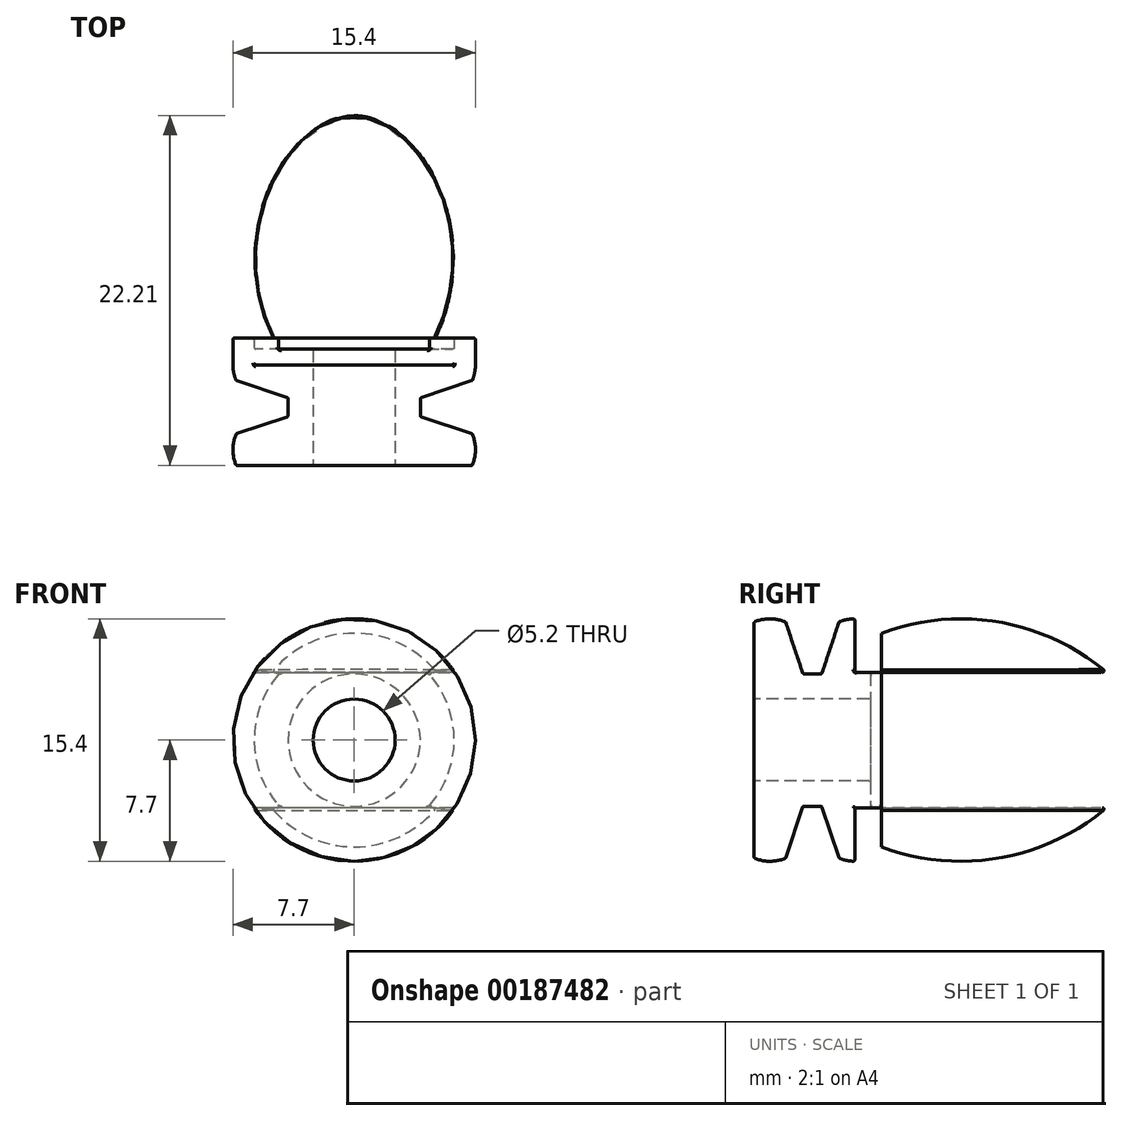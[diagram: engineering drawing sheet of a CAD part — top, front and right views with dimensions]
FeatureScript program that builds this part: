
annotation { "Feature Type Name" : "Feature", "Feature Type Description" : "" }
export const myFeature = defineFeature(function(context is Context, id is Id, definition is map)
    precondition{}
    {
        {
            var Q0;
            Q0=qCreatedBy(makeId("Front.planeOp"),FACE);
            var sketch = newSketch(context, id + "F0", { "sketchPlane" : qUnion([Q0])});
            skCircle(sketch, "E0", {"center": v(0, 0) * mm, "radius": 7.7 * mm});
            skCircle(sketch, "E1", {"center": v(0, 0) * mm, "radius": 2.6 * mm});
            skSolve(sketch);
        }
        {
            var Q0;
            Q0=qCreatedBy(makeId("Right.planeOp"),FACE);
            var sketch = newSketch(context, id + "F1", { "sketchPlane" : qUnion([Q0])});
            skLineSegment(sketch, "E2.0", {"start": v(0, -7.7) * mm, "end": v(0, 7.7) * mm, "construction": true});
            skLineSegment(sketch, "E3", {"start": v(-1.7, 7.5) * mm, "end": v(-1.7, 0) * mm});
            skLineSegment(sketch, "E4", {"start": v(-0.6, 4.2) * mm, "end": v(-0.6, 0) * mm});
            skArc(sketch, "E5", {"start": v(-1.7, 7.5) * mm, "mid": v(-2.7, 7.7) * mm, "end": v(-3.7, 7.5) * mm});
            skLineSegment(sketch, "E6", {"start": v(-0.6, 4.2) * mm, "end": v(-1.7, 7.5) * mm});
            skLineSegment(sketch, "E7", {"start": v(-12.72, 7.7) * mm, "end": v(9.43, 7.7) * mm, "construction": true});
            skLineSegment(sketch, "E8", {"start": v(-12.28, -7.7) * mm, "end": v(13.59, -7.7) * mm, "construction": true});
            skLineSegment(sketch, "E9", {"start": v(-12.4, 0) * mm, "end": v(13.31, 0) * mm, "construction": true});
            skLineSegment(sketch, "E10", {"start": v(-0.6, 4.2) * mm, "end": v(0, 4.2) * mm});
            skLineSegment(sketch, "E11", {"start": v(-3.7, 7.5) * mm, "end": v(-3.7, 0) * mm});
            skLineSegment(sketch, "E12.MirrorCS", {"start": v(0.6, 4.2) * mm, "end": v(0, 4.2) * mm});
            skLineSegment(sketch, "E13.MirrorCS", {"start": v(0.6, 4.2) * mm, "end": v(0.6, 0) * mm});
            skLineSegment(sketch, "E14.MirrorCS", {"start": v(0.6, 4.2) * mm, "end": v(1.7, 7.5) * mm});
            skLineSegment(sketch, "E15.MirrorCS", {"start": v(1.7, 7.5) * mm, "end": v(1.7, 0) * mm});
            skArc(sketch, "E16.MirrorCS", {"start": v(1.7, 7.5) * mm, "mid": v(2.7, 7.7) * mm, "end": v(3.7, 7.5) * mm});
            skLineSegment(sketch, "E17.MirrorCS", {"start": v(3.7, 7.5) * mm, "end": v(3.7, 0) * mm});
            skLineSegment(sketch, "E18", {"start": v(-3.7, 0) * mm, "end": v(-1.7, 0) * mm});
            skLineSegment(sketch, "E19", {"start": v(-1.7, 0) * mm, "end": v(-0.6, 0) * mm});
            skLineSegment(sketch, "E20", {"start": v(-0.6, 0) * mm, "end": v(0, 0) * mm});
            skLineSegment(sketch, "E21.MirrorCS", {"start": v(0.6, 0) * mm, "end": v(0, 0) * mm});
            skLineSegment(sketch, "E22.MirrorCS", {"start": v(3.7, 0) * mm, "end": v(1.7, 0) * mm});
            skLineSegment(sketch, "E23.MirrorCS", {"start": v(1.7, 0) * mm, "end": v(0.6, 0) * mm});
            skPoint(sketch, "E24", {"position": v(3.7, 6.5) * mm});
            skLineSegment(sketch, "E25", {"start": v(3.7, 4.3) * mm, "end": v(18.7, 4.3) * mm});
            skPoint(sketch, "E26", {"position": v(9.43, 7.7) * mm});
            skPoint(sketch, "E27", {"position": v(18.7, 4.3) * mm});
            skArc(sketch, "E28", {"start": v(18.7, 4.3) * mm, "mid": v(11.5, 7.55) * mm, "end": v(3.7, 6.5) * mm});
            skSolve(sketch);
        }
        {
            var Q0;
            Q0 = qSketchRegion(id + "F1", true);
            var Q1;
            Q1=sQuery(id+"F1.wireOp",EDGE,"E9");
            revolve(context, id + "F2", {"entities" : qUnion([Q0]), "axis" : qUnion([Q1]), "revolveType" : RevolveType.FULL});
        }
        {
            var Q0;
            Q0=qCreatedBy(makeId("Right.planeOp"),FACE);
            var sketch = newSketch(context, id + "F3", { "sketchPlane" : qUnion([Q0])});
            skPoint(sketch, "E29.0", {"position": v(18.7, 4.3) * mm});
            skLineSegment(sketch, "E30", {"start": v(18.7, 4.3) * mm, "end": v(18.7, 0) * mm});
            skLineSegment(sketch, "E31", {"start": v(18.7, 4.3) * mm, "end": v(3.7, 4.3) * mm});
            skPoint(sketch, "E32.0", {"position": v(3.7, 4.3) * mm});
            skPoint(sketch, "E33.0", {"position": v(3.7, 0) * mm});
            skLineSegment(sketch, "E34", {"start": v(3.7, 4.3) * mm, "end": v(3.7, 0) * mm});
            skLineSegment(sketch, "E35.MirrorCS", {"start": v(3.7, -4.3) * mm, "end": v(3.7, 0) * mm});
            skLineSegment(sketch, "E36.MirrorCS", {"start": v(18.7, -4.3) * mm, "end": v(3.7, -4.3) * mm});
            skLineSegment(sketch, "E37.MirrorCS", {"start": v(18.7, -4.3) * mm, "end": v(18.7, 0) * mm});
            skSolve(sketch);
        }
        {
            var Q0;
            Q0 = qSketchRegion(id + "F3", true);
            extrude(context, id + "F4", {"entities" : qUnion([Q0]), "operationType" : NewBodyOperationType.REMOVE, "endBound" : BoundingType.THROUGH_ALL, "oppositeDirection" : true, "depth" : 25 * mm, "hasSecondDirection" : true, "secondDirectionBound" : SecondDirectionBoundingType.THROUGH_ALL, "secondDirectionOppositeDirection" : false, "secondDirectionDepth" : 25 * mm});
        }
        {
            var Q0;
            Q0=qCreatedBy(makeId("Right.planeOp"),FACE);
            var sketch = newSketch(context, id + "F5", { "sketchPlane" : qUnion([Q0])});
            skPoint(sketch, "E38.0", {"position": v(2.7, 7.7) * mm});
            skPoint(sketch, "E39.0", {"position": v(1.7, 7.5) * mm});
            skLineSegment(sketch, "E40", {"start": v(2.7, 7.7) * mm, "end": v(4.4, 7.7) * mm});
            skLineSegment(sketch, "E41", {"start": v(4.4, 7.7) * mm, "end": v(4.4, 6.35) * mm});
            skLineSegment(sketch, "E42", {"start": v(4.4, 6.35) * mm, "end": v(2.7, 6.35) * mm});
            skLineSegment(sketch, "E43", {"start": v(2.7, 6.35) * mm, "end": v(2.7, 7.7) * mm});
            skSolve(sketch);
        }
        {
            var Q0;
            Q0 = qSketchRegion(id + "F5", true);
            var Q1;
            Q1=sQuery(id+"F1.wireOp",EDGE,"E9");
            revolve(context, id + "F6", {"entities" : qUnion([Q0]), "axis" : qUnion([Q1]), "revolveType" : RevolveType.FULL});
        }
        {
            var Q0;
            Q0=qCreatedBy(makeId("Right.planeOp"),FACE);
            var sketch = newSketch(context, id + "F7", { "sketchPlane" : qUnion([Q0])});
            skPoint(sketch, "E44.0", {"position": v(3.7, 4.3) * mm});
            skPoint(sketch, "E45.0", {"position": v(2.7, 7.7) * mm});
            skPoint(sketch, "E46.0", {"position": v(4.4, 7.7) * mm});
            skLineSegment(sketch, "E47", {"start": v(2.7, 7.7) * mm, "end": v(4.4, 7.7) * mm});
            skLineSegment(sketch, "E48", {"start": v(4.4, 4.3) * mm, "end": v(2.7, 4.3) * mm});
            skLineSegment(sketch, "E49", {"start": v(2.7, 4.3) * mm, "end": v(2.7, 7.7) * mm});
            skLineSegment(sketch, "E50", {"start": v(4.4, 7.7) * mm, "end": v(4.4, 4.3) * mm});
            skLineSegment(sketch, "E51.MirrorCS", {"start": v(4.4, -7.7) * mm, "end": v(4.4, -4.3) * mm});
            skLineSegment(sketch, "E52.MirrorCS", {"start": v(4.4, -4.3) * mm, "end": v(2.7, -4.3) * mm});
            skLineSegment(sketch, "E53.MirrorCS", {"start": v(2.7, -4.3) * mm, "end": v(2.7, -7.7) * mm});
            skLineSegment(sketch, "E54.MirrorCS", {"start": v(2.7, -7.7) * mm, "end": v(4.4, -7.7) * mm});
            skSolve(sketch);
        }
        {
            var Q0;
            Q0 = qSketchRegion(id + "F7", true);
            extrude(context, id + "F8", {"entities" : qUnion([Q0]), "operationType" : NewBodyOperationType.REMOVE, "endBound" : BoundingType.THROUGH_ALL, "depth" : 25 * mm, "hasSecondDirection" : true, "secondDirectionBound" : SecondDirectionBoundingType.THROUGH_ALL, "secondDirectionOppositeDirection" : true, "secondDirectionDepth" : 25 * mm});
        }
        {
            var Q0;
            Q0=makeQuery(id+"F2.opRevolve","SWEPT_BODY",BODY,{"disambiguationData":[OSD([sQuery(id+"F1.wireOp",EDGE,"E5"),sQuery(id+"F1.wireOp",EDGE,"E6"),sQuery(id+"F1.wireOp",EDGE,"E10"),sQuery(id+"F1.wireOp",EDGE,"E11"),sQuery(id+"F1.wireOp",EDGE,"E12.MirrorCS"),sQuery(id+"F1.wireOp",EDGE,"E14.MirrorCS"),sQuery(id+"F1.wireOp",EDGE,"E16.MirrorCS"),sQuery(id+"F1.wireOp",EDGE,"E17.MirrorCS"),sQuery(id+"F1.wireOp",EDGE,"E18"),sQuery(id+"F1.wireOp",EDGE,"E19"),sQuery(id+"F1.wireOp",EDGE,"E20"),sQuery(id+"F1.wireOp",EDGE,"E21.MirrorCS"),sQuery(id+"F1.wireOp",EDGE,"E22.MirrorCS"),sQuery(id+"F1.wireOp",EDGE,"E23.MirrorCS"),sQuery(id+"F1.wireOp",EDGE,"E25"),sQuery(id+"F1.wireOp",EDGE,"E28")])]});
            var Q1;
            Q1=makeQuery(id+"F8.boolean.opBoolean","SPLIT",BODY,{"disambiguationData":[OD(1.0)],"derivedFrom":makeQuery(id+"F6.opRevolve","SWEPT_BODY",BODY,{"disambiguationData":[OSD([sQuery(id+"F5.wireOp",EDGE,"E40"),sQuery(id+"F5.wireOp",EDGE,"E41"),sQuery(id+"F5.wireOp",EDGE,"E42"),sQuery(id+"F5.wireOp",EDGE,"E43")])]})});
            var Q2;
            Q2=makeQuery(id+"F8.boolean.opBoolean","SPLIT",BODY,{"disambiguationData":[OD(0.0)],"derivedFrom":makeQuery(id+"F6.opRevolve","SWEPT_BODY",BODY,{"disambiguationData":[OSD([sQuery(id+"F5.wireOp",EDGE,"E40"),sQuery(id+"F5.wireOp",EDGE,"E41"),sQuery(id+"F5.wireOp",EDGE,"E42"),sQuery(id+"F5.wireOp",EDGE,"E43")])]})});
            booleanBodies(context, id + "F9", {"operationType" : BooleanOperationType.UNION, "tools" : qUnion([Q0, Q1, Q2])});
        }
        {
            var Q0;
            Q0=makeQuery(id+"F0.imprint","IMPRINT",FACE,{"disambiguationData":[TD([[makeQuery(id+"F0.imprint","IMPRINT",EDGE,{"derivedFrom":sQuery(id+"F0.wireOp",EDGE,"E1")}),1.0]])]});
            extrude(context, id + "F10", {"entities" : qUnion([Q0]), "operationType" : NewBodyOperationType.REMOVE, "endBound" : BoundingType.THROUGH_ALL, "oppositeDirection" : true, "depth" : 25 * mm, "hasSecondDirection" : true, "secondDirectionBound" : SecondDirectionBoundingType.THROUGH_ALL, "secondDirectionOppositeDirection" : false, "secondDirectionDepth" : 25 * mm});
        }
        {
            var Q0;
            {var subQ0=sQuery(id+"F1.wireOp",EDGE,"E16.MirrorCS");var subQ2=makeQuery(id+"F8.opExtrude","SWEPT_FACE",FACE,{"disambiguationData":[OSD([sQuery(id+"F7.wireOp",EDGE,"E48")])]});var subQ3=sQuery(id+"F1.wireOp",EDGE,"E17.MirrorCS");Q0=makeQuery(id+"F9.opBoolean","SPLIT",FACE,{"disambiguationData":[TD([makeQuery(id+"F8.boolean.opBoolean","COPY",FACE,{"disambiguationData":[OD(0.0)],"derivedFrom":subQ2})])],"derivedFrom":makeQuery(id+"F4.boolean.opBoolean","MERGE",FACE,{"derivedFrom":[makeQuery(id+"F2.opRevolve","SWEPT_FACE",FACE,{"disambiguationData":[OSD([subQ3]),TDD([makeQuery(id+"F1.imprint","IMPRINT",EDGE,{"disambiguationData":[TD([[makeQuery(id+"F1.imprint","INTERSECT",VERTEX,{"derivedFrom":[subQ0,subQ3]}),-1.0]])],"derivedFrom":subQ3})])]}),makeQuery(id+"F2.opRevolve","SWEPT_FACE",FACE,{"disambiguationData":[OSD([subQ3]),TDD([makeQuery(id+"F1.imprint","IMPRINT",EDGE,{"disambiguationData":[TD([[makeQuery(id+"F1.imprint","INTERSECT",VERTEX,{"derivedFrom":[subQ3,sQuery(id+"F1.wireOp",EDGE,"E22.MirrorCS")]}),1.0]])],"derivedFrom":subQ3})])]}),makeQuery(id+"F4.opExtrude","SWEPT_FACE",FACE,{"disambiguationData":[OSD([sQuery(id+"F3.wireOp",EDGE,"E34"),sQuery(id+"F3.wireOp",EDGE,"E35.MirrorCS")])]})]})});}
            var Q1;
            Q1=makeQuery(id+"F2.opRevolve","SWEPT_FACE",FACE,{"disambiguationData":[OSD([sQuery(id+"F1.wireOp",EDGE,"E16.MirrorCS")])]});
            var Q2;
            Q2=makeQuery(id+"F8.boolean.opBoolean","SPLIT",FACE,{"disambiguationData":[OD(1.0)],"derivedFrom":makeQuery(id+"F6.opRevolve","SWEPT_FACE",FACE,{"disambiguationData":[OSD([sQuery(id+"F5.wireOp",EDGE,"E40")])]})});
            var Q3;
            Q3=makeQuery(id+"F8.boolean.opBoolean","COPY",FACE,{"disambiguationData":[OD(1.0)],"derivedFrom":makeQuery(id+"F8.opExtrude","SWEPT_FACE",FACE,{"disambiguationData":[OSD([sQuery(id+"F7.wireOp",EDGE,"E48")])]})});
            var Q4;
            Q4=makeQuery(id+"F8.boolean.opBoolean","SPLIT",FACE,{"disambiguationData":[OD(1.0)],"derivedFrom":makeQuery(id+"F6.opRevolve","SWEPT_FACE",FACE,{"disambiguationData":[OSD([sQuery(id+"F5.wireOp",EDGE,"E41")])]})});
            var Q5;
            {var subQ0=makeQuery(id+"F8.opExtrude","SWEPT_FACE",FACE,{"disambiguationData":[OSD([sQuery(id+"F7.wireOp",EDGE,"E48")])]});var subQ1=makeQuery(id+"F2.opRevolve","SWEPT_FACE",FACE,{"disambiguationData":[OSD([sQuery(id+"F1.wireOp",EDGE,"E28")])]});var subQ2=makeQuery(id+"F4.opExtrude","SWEPT_FACE",FACE,{"disambiguationData":[OSD([sQuery(id+"F3.wireOp",EDGE,"E31")])]});Q5=makeQuery(id+"F9.opBoolean","SPLIT",EDGE,{"disambiguationData":[TD([subQ1,makeQuery(id+"F4.boolean.opBoolean","COPY",FACE,{"derivedFrom":subQ2}),makeQuery(id+"F6.opRevolve","SWEPT_FACE",FACE,{"disambiguationData":[OSD([sQuery(id+"F5.wireOp",EDGE,"E41")])]}),makeQuery(id+"F8.boolean.opBoolean","COPY",FACE,{"disambiguationData":[OD(0.0)],"derivedFrom":subQ0}),makeQuery(id+"F8.boolean.opBoolean","COPY",FACE,{"disambiguationData":[OD(1.0)],"derivedFrom":subQ0})])],"derivedFrom":makeQuery(id+"F4.boolean.opBoolean","INTERSECT",EDGE,{"derivedFrom":[subQ1,subQ2]})});}
            var Q6;
            Q6=makeQuery(id+"F2.opRevolve","SWEPT_EDGE",EDGE,{"disambiguationData":[OSD([sQuery(id+"F1.wireOp",EDGE,"E5"),sQuery(id+"F1.wireOp",EDGE,"E11")])]});
            var Q7;
            Q7=makeQuery(id+"F2.opRevolve","SWEPT_EDGE",EDGE,{"disambiguationData":[OSD([sQuery(id+"F1.wireOp",EDGE,"E14.MirrorCS"),sQuery(id+"F1.wireOp",EDGE,"E15.MirrorCS"),sQuery(id+"F1.wireOp",EDGE,"E16.MirrorCS")])]});
            var Q8;
            Q8=makeQuery(id+"F2.opRevolve","SWEPT_EDGE",EDGE,{"disambiguationData":[OSD([sQuery(id+"F1.wireOp",EDGE,"E3"),sQuery(id+"F1.wireOp",EDGE,"E5"),sQuery(id+"F1.wireOp",EDGE,"E6")])]});
            var Q9;
            Q9=makeQuery(id+"F2.opRevolve","SWEPT_EDGE",EDGE,{"disambiguationData":[OSD([sQuery(id+"F1.wireOp",EDGE,"E4"),sQuery(id+"F1.wireOp",EDGE,"E6"),sQuery(id+"F1.wireOp",EDGE,"E10")])]});
            var Q10;
            Q10=makeQuery(id+"F2.opRevolve","SWEPT_EDGE",EDGE,{"disambiguationData":[OSD([sQuery(id+"F1.wireOp",EDGE,"E12.MirrorCS"),sQuery(id+"F1.wireOp",EDGE,"E13.MirrorCS"),sQuery(id+"F1.wireOp",EDGE,"E14.MirrorCS")])]});
            var Q11;
            Q11=makeQuery(id+"F10.boolean.opBoolean","INTERSECT",EDGE,{"derivedFrom":[makeQuery(id+"F2.opRevolve","SWEPT_FACE",FACE,{"disambiguationData":[OSD([sQuery(id+"F1.wireOp",EDGE,"E11")])]}),makeQuery(id+"F10.opExtrude","SWEPT_FACE",FACE,{"disambiguationData":[OSD([sQuery(id+"F0.wireOp",EDGE,"E1")])]})]});
            var Q12;
            Q12=makeQuery(id+"F9.opBoolean","INTERSECT",EDGE,{"derivedFrom":[makeQuery(id+"F2.opRevolve","SWEPT_FACE",FACE,{"disambiguationData":[OSD([sQuery(id+"F1.wireOp",EDGE,"E16.MirrorCS")])]}),makeQuery(id+"F8.boolean.opBoolean","SPLIT",FACE,{"disambiguationData":[OD(1.0)],"derivedFrom":makeQuery(id+"F6.opRevolve","SWEPT_FACE",FACE,{"disambiguationData":[OSD([sQuery(id+"F5.wireOp",EDGE,"E40")])]})})]});
            var Q13;
            Q13=makeQuery(id+"F8.boolean.opBoolean","SPLIT",EDGE,{"disambiguationData":[OD(1.0)],"derivedFrom":makeQuery(id+"F6.opRevolve","SWEPT_EDGE",EDGE,{"disambiguationData":[OSD([sQuery(id+"F5.wireOp",EDGE,"E40"),sQuery(id+"F5.wireOp",EDGE,"E41")])]})});
            var Q14;
            {var subQ0=sQuery(id+"F1.wireOp",EDGE,"E17.MirrorCS");var subQ1=sQuery(id+"F1.wireOp",EDGE,"E16.MirrorCS");var subQ2=makeQuery(id+"F8.opExtrude","SWEPT_FACE",FACE,{"disambiguationData":[OSD([sQuery(id+"F7.wireOp",EDGE,"E48")])]});Q14=makeQuery(id+"F9.opBoolean","SPLIT",EDGE,{"disambiguationData":[TD([makeQuery(id+"F8.boolean.opBoolean","COPY",FACE,{"disambiguationData":[OD(0.0)],"derivedFrom":subQ2})])],"derivedFrom":makeQuery(id+"F2.opRevolve","SWEPT_EDGE",EDGE,{"disambiguationData":[OSD([subQ1,subQ0])]})});}
            var Q15;
            {var subQ0=sQuery(id+"F1.wireOp",EDGE,"E17.MirrorCS");var subQ1=sQuery(id+"F1.wireOp",EDGE,"E16.MirrorCS");var subQ2=makeQuery(id+"F8.opExtrude","SWEPT_FACE",FACE,{"disambiguationData":[OSD([sQuery(id+"F7.wireOp",EDGE,"E52.MirrorCS")])]});Q15=makeQuery(id+"F9.opBoolean","SPLIT",EDGE,{"disambiguationData":[TD([makeQuery(id+"F8.boolean.opBoolean","COPY",FACE,{"disambiguationData":[OD(0.0)],"derivedFrom":subQ2})])],"derivedFrom":makeQuery(id+"F2.opRevolve","SWEPT_EDGE",EDGE,{"disambiguationData":[OSD([subQ1,subQ0])]})});}
            var Q16;
            {var subQ0=makeQuery(id+"F8.opExtrude","SWEPT_FACE",FACE,{"disambiguationData":[OSD([sQuery(id+"F7.wireOp",EDGE,"E52.MirrorCS")])]});var subQ1=makeQuery(id+"F4.opExtrude","SWEPT_FACE",FACE,{"disambiguationData":[OSD([sQuery(id+"F3.wireOp",EDGE,"E36.MirrorCS")])]});var subQ2=makeQuery(id+"F2.opRevolve","SWEPT_FACE",FACE,{"disambiguationData":[OSD([sQuery(id+"F1.wireOp",EDGE,"E28")])]});Q16=makeQuery(id+"F9.opBoolean","SPLIT",EDGE,{"disambiguationData":[TD([subQ2,makeQuery(id+"F4.boolean.opBoolean","COPY",FACE,{"derivedFrom":subQ1}),makeQuery(id+"F6.opRevolve","SWEPT_FACE",FACE,{"disambiguationData":[OSD([sQuery(id+"F5.wireOp",EDGE,"E41")])]}),makeQuery(id+"F8.boolean.opBoolean","COPY",FACE,{"disambiguationData":[OD(0.0)],"derivedFrom":subQ0}),makeQuery(id+"F8.boolean.opBoolean","COPY",FACE,{"disambiguationData":[OD(1.0)],"derivedFrom":subQ0})])],"derivedFrom":makeQuery(id+"F4.boolean.opBoolean","INTERSECT",EDGE,{"derivedFrom":[subQ2,subQ1]})});}
            var Q17;
            Q17=makeQuery(id+"F4.boolean.opBoolean","COPY",EDGE,{"derivedFrom":makeQuery(id+"F4.opExtrude","SWEPT_EDGE",EDGE,{"disambiguationData":[OSD([sQuery(id+"F3.wireOp",EDGE,"E35.MirrorCS"),sQuery(id+"F3.wireOp",EDGE,"E36.MirrorCS")])]})});
            var Q18;
            Q18=makeQuery(id+"F8.boolean.opBoolean","SPLIT",EDGE,{"disambiguationData":[OD(0.0)],"derivedFrom":makeQuery(id+"F6.opRevolve","SWEPT_EDGE",EDGE,{"disambiguationData":[OSD([sQuery(id+"F5.wireOp",EDGE,"E41"),sQuery(id+"F5.wireOp",EDGE,"E42")])]})});
            var Q19;
            Q19=makeQuery(id+"F8.boolean.opBoolean","SPLIT",EDGE,{"disambiguationData":[OD(1.0)],"derivedFrom":makeQuery(id+"F6.opRevolve","SWEPT_EDGE",EDGE,{"disambiguationData":[OSD([sQuery(id+"F5.wireOp",EDGE,"E41"),sQuery(id+"F5.wireOp",EDGE,"E42")])]})});
            var Q20;
            Q20=makeQuery(id+"F4.boolean.opBoolean","COPY",EDGE,{"derivedFrom":makeQuery(id+"F4.opExtrude","SWEPT_EDGE",EDGE,{"disambiguationData":[OSD([sQuery(id+"F3.wireOp",EDGE,"E31"),sQuery(id+"F3.wireOp",EDGE,"E34")])]})});
            var Q21;
            Q21=makeQuery(id+"F9.opBoolean","INTERSECT",EDGE,{"derivedFrom":[makeQuery(id+"F2.opRevolve","SWEPT_FACE",FACE,{"disambiguationData":[OSD([sQuery(id+"F1.wireOp",EDGE,"E16.MirrorCS")])]}),makeQuery(id+"F8.boolean.opBoolean","SPLIT",FACE,{"disambiguationData":[OD(0.0)],"derivedFrom":makeQuery(id+"F6.opRevolve","SWEPT_FACE",FACE,{"disambiguationData":[OSD([sQuery(id+"F5.wireOp",EDGE,"E40")])]})})]});
            var Q22;
            Q22=makeQuery(id+"F9.opBoolean","INTERSECT",EDGE,{"derivedFrom":[makeQuery(id+"F2.opRevolve","SWEPT_FACE",FACE,{"disambiguationData":[OSD([sQuery(id+"F1.wireOp",EDGE,"E16.MirrorCS")])]}),makeQuery(id+"F8.boolean.opBoolean","COPY",FACE,{"disambiguationData":[OD(1.0)],"derivedFrom":makeQuery(id+"F8.opExtrude","SWEPT_FACE",FACE,{"disambiguationData":[OSD([sQuery(id+"F7.wireOp",EDGE,"E48")])]})})]});
            var Q23;
            {var subQ0=sQuery(id+"F7.wireOp",EDGE,"E48");Q23=makeQuery(id+"F9.opBoolean","SPLIT",EDGE,{"disambiguationData":[TD([makeQuery(id+"F6.opRevolve","SWEPT_FACE",FACE,{"disambiguationData":[OSD([sQuery(id+"F5.wireOp",EDGE,"E40")])]})])],"derivedFrom":makeQuery(id+"F8.boolean.opBoolean","COPY",EDGE,{"disambiguationData":[OD(1.0)],"derivedFrom":makeQuery(id+"F8.opExtrude","SWEPT_EDGE",EDGE,{"disambiguationData":[OSD([subQ0,sQuery(id+"F7.wireOp",EDGE,"E50")])]})})});}
            var Q24;
            Q24=makeQuery(id+"F8.boolean.opBoolean","INTERSECT",EDGE,{"disambiguationData":[OD(1.0)],"derivedFrom":[makeQuery(id+"F6.opRevolve","SWEPT_FACE",FACE,{"disambiguationData":[OSD([sQuery(id+"F5.wireOp",EDGE,"E40")])]}),makeQuery(id+"F8.opExtrude","SWEPT_FACE",FACE,{"disambiguationData":[OSD([sQuery(id+"F7.wireOp",EDGE,"E48")])]})]});
            var Q25;
            {var subQ0=sQuery(id+"F1.wireOp",EDGE,"E28");var subQ1=sQuery(id+"F1.wireOp",EDGE,"E17.MirrorCS");Q25=makeQuery(id+"F4.boolean.opBoolean","SPLIT",EDGE,{"disambiguationData":[TD([makeQuery(id+"F4.opExtrude","SWEPT_FACE",FACE,{"disambiguationData":[OSD([sQuery(id+"F3.wireOp",EDGE,"E36.MirrorCS")])]})])],"derivedFrom":makeQuery(id+"F2.opRevolve","SWEPT_EDGE",EDGE,{"disambiguationData":[OSD([subQ1,subQ0])]})});}
            var Q26;
            {var subQ0=sQuery(id+"F1.wireOp",EDGE,"E28");var subQ1=sQuery(id+"F1.wireOp",EDGE,"E17.MirrorCS");Q26=makeQuery(id+"F4.boolean.opBoolean","SPLIT",EDGE,{"disambiguationData":[TD([makeQuery(id+"F4.opExtrude","SWEPT_FACE",FACE,{"disambiguationData":[OSD([sQuery(id+"F3.wireOp",EDGE,"E31")])]})])],"derivedFrom":makeQuery(id+"F2.opRevolve","SWEPT_EDGE",EDGE,{"disambiguationData":[OSD([subQ1,subQ0])]})});}
            var Q27;
            Q27=makeQuery(id+"F9.opBoolean","INTERSECT",EDGE,{"derivedFrom":[makeQuery(id+"F2.opRevolve","SWEPT_FACE",FACE,{"disambiguationData":[OSD([sQuery(id+"F1.wireOp",EDGE,"E16.MirrorCS")])]}),makeQuery(id+"F8.boolean.opBoolean","COPY",FACE,{"disambiguationData":[OD(1.0)],"derivedFrom":makeQuery(id+"F8.opExtrude","SWEPT_FACE",FACE,{"disambiguationData":[OSD([sQuery(id+"F7.wireOp",EDGE,"E52.MirrorCS")])]})})]});
            var Q28;
            {var subQ0=sQuery(id+"F1.wireOp",EDGE,"E17.MirrorCS");Q28=makeQuery(id+"F9.opBoolean","INTERSECT",EDGE,{"derivedFrom":[makeQuery(id+"F4.boolean.opBoolean","MERGE",FACE,{"derivedFrom":[makeQuery(id+"F2.opRevolve","SWEPT_FACE",FACE,{"disambiguationData":[OSD([subQ0]),TDD([makeQuery(id+"F1.imprint","IMPRINT",EDGE,{"disambiguationData":[TD([[makeQuery(id+"F1.imprint","INTERSECT",VERTEX,{"derivedFrom":[sQuery(id+"F1.wireOp",EDGE,"E16.MirrorCS"),subQ0]}),-1.0]])],"derivedFrom":subQ0})])]}),makeQuery(id+"F2.opRevolve","SWEPT_FACE",FACE,{"disambiguationData":[OSD([subQ0]),TDD([makeQuery(id+"F1.imprint","IMPRINT",EDGE,{"disambiguationData":[TD([[makeQuery(id+"F1.imprint","INTERSECT",VERTEX,{"derivedFrom":[subQ0,sQuery(id+"F1.wireOp",EDGE,"E22.MirrorCS")]}),1.0]])],"derivedFrom":subQ0})])]}),makeQuery(id+"F4.opExtrude","SWEPT_FACE",FACE,{"disambiguationData":[OSD([sQuery(id+"F3.wireOp",EDGE,"E34"),sQuery(id+"F3.wireOp",EDGE,"E35.MirrorCS")])]})]}),makeQuery(id+"F8.boolean.opBoolean","SPLIT",FACE,{"disambiguationData":[OD(0.0)],"derivedFrom":makeQuery(id+"F6.opRevolve","SWEPT_FACE",FACE,{"disambiguationData":[OSD([sQuery(id+"F5.wireOp",EDGE,"E42")])]})})]});}
            var Q29;
            {var subQ0=sQuery(id+"F1.wireOp",EDGE,"E17.MirrorCS");Q29=makeQuery(id+"F9.opBoolean","INTERSECT",EDGE,{"derivedFrom":[makeQuery(id+"F4.boolean.opBoolean","MERGE",FACE,{"derivedFrom":[makeQuery(id+"F2.opRevolve","SWEPT_FACE",FACE,{"disambiguationData":[OSD([subQ0]),TDD([makeQuery(id+"F1.imprint","IMPRINT",EDGE,{"disambiguationData":[TD([[makeQuery(id+"F1.imprint","INTERSECT",VERTEX,{"derivedFrom":[sQuery(id+"F1.wireOp",EDGE,"E16.MirrorCS"),subQ0]}),-1.0]])],"derivedFrom":subQ0})])]}),makeQuery(id+"F2.opRevolve","SWEPT_FACE",FACE,{"disambiguationData":[OSD([subQ0]),TDD([makeQuery(id+"F1.imprint","IMPRINT",EDGE,{"disambiguationData":[TD([[makeQuery(id+"F1.imprint","INTERSECT",VERTEX,{"derivedFrom":[subQ0,sQuery(id+"F1.wireOp",EDGE,"E22.MirrorCS")]}),1.0]])],"derivedFrom":subQ0})])]}),makeQuery(id+"F4.opExtrude","SWEPT_FACE",FACE,{"disambiguationData":[OSD([sQuery(id+"F3.wireOp",EDGE,"E34"),sQuery(id+"F3.wireOp",EDGE,"E35.MirrorCS")])]})]}),makeQuery(id+"F8.boolean.opBoolean","SPLIT",FACE,{"disambiguationData":[OD(1.0)],"derivedFrom":makeQuery(id+"F6.opRevolve","SWEPT_FACE",FACE,{"disambiguationData":[OSD([sQuery(id+"F5.wireOp",EDGE,"E42")])]})})]});}
            var Q30;
            {var subQ0=sQuery(id+"F1.wireOp",EDGE,"E28");var subQ1=makeQuery(id+"F2.opRevolve","SWEPT_FACE",FACE,{"disambiguationData":[OSD([subQ0])]});var subQ2=sQuery(id+"F1.wireOp",EDGE,"E17.MirrorCS");var subQ3=makeQuery(id+"F4.opExtrude","SWEPT_FACE",FACE,{"disambiguationData":[OSD([sQuery(id+"F3.wireOp",EDGE,"E31")])]});Q30=makeQuery(id+"F9.opBoolean","SPLIT",EDGE,{"disambiguationData":[TD([makeQuery(id+"F2.opRevolve","SWEPT_FACE",FACE,{"disambiguationData":[OSD([subQ2]),TDD([makeQuery(id+"F1.imprint","IMPRINT",EDGE,{"disambiguationData":[TD([[makeQuery(id+"F1.imprint","INTERSECT",VERTEX,{"derivedFrom":[sQuery(id+"F1.wireOp",EDGE,"E16.MirrorCS"),subQ2]}),-1.0]])],"derivedFrom":subQ2})])]}),makeQuery(id+"F2.opRevolve","SWEPT_FACE",FACE,{"disambiguationData":[OSD([subQ2]),TDD([makeQuery(id+"F1.imprint","IMPRINT",EDGE,{"disambiguationData":[TD([[makeQuery(id+"F1.imprint","INTERSECT",VERTEX,{"derivedFrom":[subQ2,sQuery(id+"F1.wireOp",EDGE,"E22.MirrorCS")]}),1.0]])],"derivedFrom":subQ2})])]}),subQ1,makeQuery(id+"F4.opExtrude","SWEPT_FACE",FACE,{"disambiguationData":[OSD([sQuery(id+"F3.wireOp",EDGE,"E34"),sQuery(id+"F3.wireOp",EDGE,"E35.MirrorCS")])]}),makeQuery(id+"F4.boolean.opBoolean","COPY",FACE,{"derivedFrom":subQ3}),makeQuery(id+"F6.opRevolve","SWEPT_FACE",FACE,{"disambiguationData":[OSD([sQuery(id+"F5.wireOp",EDGE,"E41")])]}),makeQuery(id+"F8.boolean.opBoolean","COPY",FACE,{"disambiguationData":[OD(1.0)],"derivedFrom":makeQuery(id+"F8.opExtrude","SWEPT_FACE",FACE,{"disambiguationData":[OSD([sQuery(id+"F7.wireOp",EDGE,"E48")])]})})])],"derivedFrom":makeQuery(id+"F4.boolean.opBoolean","INTERSECT",EDGE,{"derivedFrom":[subQ1,subQ3]})});}
            var Q31;
            {var subQ0=sQuery(id+"F1.wireOp",EDGE,"E17.MirrorCS");Q31=makeQuery(id+"F10.boolean.opBoolean","INTERSECT",EDGE,{"derivedFrom":[makeQuery(id+"F9.opBoolean","SPLIT",FACE,{"disambiguationData":[TD([makeQuery(id+"F4.boolean.opBoolean","COPY",FACE,{"derivedFrom":makeQuery(id+"F4.opExtrude","SWEPT_FACE",FACE,{"disambiguationData":[OSD([sQuery(id+"F3.wireOp",EDGE,"E31")])]})})])],"derivedFrom":makeQuery(id+"F4.boolean.opBoolean","MERGE",FACE,{"derivedFrom":[makeQuery(id+"F2.opRevolve","SWEPT_FACE",FACE,{"disambiguationData":[OSD([subQ0]),TDD([makeQuery(id+"F1.imprint","IMPRINT",EDGE,{"disambiguationData":[TD([[makeQuery(id+"F1.imprint","INTERSECT",VERTEX,{"derivedFrom":[sQuery(id+"F1.wireOp",EDGE,"E16.MirrorCS"),subQ0]}),-1.0]])],"derivedFrom":subQ0})])]}),makeQuery(id+"F2.opRevolve","SWEPT_FACE",FACE,{"disambiguationData":[OSD([subQ0]),TDD([makeQuery(id+"F1.imprint","IMPRINT",EDGE,{"disambiguationData":[TD([[makeQuery(id+"F1.imprint","INTERSECT",VERTEX,{"derivedFrom":[subQ0,sQuery(id+"F1.wireOp",EDGE,"E22.MirrorCS")]}),1.0]])],"derivedFrom":subQ0})])]}),makeQuery(id+"F4.opExtrude","SWEPT_FACE",FACE,{"disambiguationData":[OSD([sQuery(id+"F3.wireOp",EDGE,"E34"),sQuery(id+"F3.wireOp",EDGE,"E35.MirrorCS")])]})]})}),makeQuery(id+"F10.opExtrude","SWEPT_FACE",FACE,{"disambiguationData":[OSD([sQuery(id+"F0.wireOp",EDGE,"E1")])]})]});}
            var Q32;
            {var subQ0=sQuery(id+"F1.wireOp",EDGE,"E17.MirrorCS");Q32=makeQuery(id+"F9.opBoolean","INTERSECT",EDGE,{"derivedFrom":[makeQuery(id+"F4.boolean.opBoolean","MERGE",FACE,{"derivedFrom":[makeQuery(id+"F2.opRevolve","SWEPT_FACE",FACE,{"disambiguationData":[OSD([subQ0]),TDD([makeQuery(id+"F1.imprint","IMPRINT",EDGE,{"disambiguationData":[TD([[makeQuery(id+"F1.imprint","INTERSECT",VERTEX,{"derivedFrom":[sQuery(id+"F1.wireOp",EDGE,"E16.MirrorCS"),subQ0]}),-1.0]])],"derivedFrom":subQ0})])]}),makeQuery(id+"F2.opRevolve","SWEPT_FACE",FACE,{"disambiguationData":[OSD([subQ0]),TDD([makeQuery(id+"F1.imprint","IMPRINT",EDGE,{"disambiguationData":[TD([[makeQuery(id+"F1.imprint","INTERSECT",VERTEX,{"derivedFrom":[subQ0,sQuery(id+"F1.wireOp",EDGE,"E22.MirrorCS")]}),1.0]])],"derivedFrom":subQ0})])]}),makeQuery(id+"F4.opExtrude","SWEPT_FACE",FACE,{"disambiguationData":[OSD([sQuery(id+"F3.wireOp",EDGE,"E34"),sQuery(id+"F3.wireOp",EDGE,"E35.MirrorCS")])]})]}),makeQuery(id+"F8.boolean.opBoolean","COPY",FACE,{"disambiguationData":[OD(1.0)],"derivedFrom":makeQuery(id+"F8.opExtrude","SWEPT_FACE",FACE,{"disambiguationData":[OSD([sQuery(id+"F7.wireOp",EDGE,"E48")])]})})]});}
            var Q33;
            Q33=makeQuery(id+"F9.opBoolean","INTERSECT",EDGE,{"derivedFrom":[makeQuery(id+"F2.opRevolve","SWEPT_FACE",FACE,{"disambiguationData":[OSD([sQuery(id+"F1.wireOp",EDGE,"E16.MirrorCS")])]}),makeQuery(id+"F8.boolean.opBoolean","COPY",FACE,{"disambiguationData":[OD(0.0)],"derivedFrom":makeQuery(id+"F8.opExtrude","SWEPT_FACE",FACE,{"disambiguationData":[OSD([sQuery(id+"F7.wireOp",EDGE,"E52.MirrorCS")])]})})]});
            var Q34;
            {var subQ0=sQuery(id+"F7.wireOp",EDGE,"E48");Q34=makeQuery(id+"F9.opBoolean","SPLIT",EDGE,{"disambiguationData":[TD([makeQuery(id+"F6.opRevolve","SWEPT_FACE",FACE,{"disambiguationData":[OSD([sQuery(id+"F5.wireOp",EDGE,"E42")])]})])],"derivedFrom":makeQuery(id+"F8.boolean.opBoolean","COPY",EDGE,{"disambiguationData":[OD(1.0)],"derivedFrom":makeQuery(id+"F8.opExtrude","SWEPT_EDGE",EDGE,{"disambiguationData":[OSD([subQ0,sQuery(id+"F7.wireOp",EDGE,"E50")])]})})});}
            var Q35;
            Q35=makeQuery(id+"F8.boolean.opBoolean","INTERSECT",EDGE,{"disambiguationData":[OD(0.0)],"derivedFrom":[makeQuery(id+"F6.opRevolve","SWEPT_FACE",FACE,{"disambiguationData":[OSD([sQuery(id+"F5.wireOp",EDGE,"E40")])]}),makeQuery(id+"F8.opExtrude","SWEPT_FACE",FACE,{"disambiguationData":[OSD([sQuery(id+"F7.wireOp",EDGE,"E48")])]})]});
            var Q36;
            Q36=makeQuery(id+"F8.boolean.opBoolean","SPLIT",EDGE,{"disambiguationData":[OD(0.0)],"derivedFrom":makeQuery(id+"F6.opRevolve","SWEPT_EDGE",EDGE,{"disambiguationData":[OSD([sQuery(id+"F5.wireOp",EDGE,"E40"),sQuery(id+"F5.wireOp",EDGE,"E41")])]})});
            var Q37;
            Q37=makeQuery(id+"F8.boolean.opBoolean","INTERSECT",EDGE,{"disambiguationData":[OD(0.0)],"derivedFrom":[makeQuery(id+"F6.opRevolve","SWEPT_FACE",FACE,{"disambiguationData":[OSD([sQuery(id+"F5.wireOp",EDGE,"E42")])]}),makeQuery(id+"F8.opExtrude","SWEPT_FACE",FACE,{"disambiguationData":[OSD([sQuery(id+"F7.wireOp",EDGE,"E48")])]})]});
            var Q38;
            Q38=makeQuery(id+"F9.opBoolean","INTERSECT",EDGE,{"derivedFrom":[makeQuery(id+"F2.opRevolve","SWEPT_FACE",FACE,{"disambiguationData":[OSD([sQuery(id+"F1.wireOp",EDGE,"E16.MirrorCS")])]}),makeQuery(id+"F8.boolean.opBoolean","COPY",FACE,{"disambiguationData":[OD(0.0)],"derivedFrom":makeQuery(id+"F8.opExtrude","SWEPT_FACE",FACE,{"disambiguationData":[OSD([sQuery(id+"F7.wireOp",EDGE,"E48")])]})})]});
            var Q39;
            Q39=makeQuery(id+"F8.boolean.opBoolean","INTERSECT",EDGE,{"disambiguationData":[OD(0.0)],"derivedFrom":[makeQuery(id+"F6.opRevolve","SWEPT_FACE",FACE,{"disambiguationData":[OSD([sQuery(id+"F5.wireOp",EDGE,"E40")])]}),makeQuery(id+"F8.opExtrude","SWEPT_FACE",FACE,{"disambiguationData":[OSD([sQuery(id+"F7.wireOp",EDGE,"E52.MirrorCS")])]})]});
            var Q40;
            Q40=makeQuery(id+"F8.boolean.opBoolean","INTERSECT",EDGE,{"disambiguationData":[OD(1.0)],"derivedFrom":[makeQuery(id+"F6.opRevolve","SWEPT_FACE",FACE,{"disambiguationData":[OSD([sQuery(id+"F5.wireOp",EDGE,"E42")])]}),makeQuery(id+"F8.opExtrude","SWEPT_FACE",FACE,{"disambiguationData":[OSD([sQuery(id+"F7.wireOp",EDGE,"E48")])]})]});
            var Q41;
            Q41=makeQuery(id+"F8.boolean.opBoolean","INTERSECT",EDGE,{"disambiguationData":[OD(0.0)],"derivedFrom":[makeQuery(id+"F6.opRevolve","SWEPT_FACE",FACE,{"disambiguationData":[OSD([sQuery(id+"F5.wireOp",EDGE,"E42")])]}),makeQuery(id+"F8.opExtrude","SWEPT_FACE",FACE,{"disambiguationData":[OSD([sQuery(id+"F7.wireOp",EDGE,"E52.MirrorCS")])]})]});
            var Q42;
            {var subQ0=sQuery(id+"F1.wireOp",EDGE,"E17.MirrorCS");Q42=makeQuery(id+"F9.opBoolean","INTERSECT",EDGE,{"derivedFrom":[makeQuery(id+"F4.boolean.opBoolean","MERGE",FACE,{"derivedFrom":[makeQuery(id+"F2.opRevolve","SWEPT_FACE",FACE,{"disambiguationData":[OSD([subQ0]),TDD([makeQuery(id+"F1.imprint","IMPRINT",EDGE,{"disambiguationData":[TD([[makeQuery(id+"F1.imprint","INTERSECT",VERTEX,{"derivedFrom":[sQuery(id+"F1.wireOp",EDGE,"E16.MirrorCS"),subQ0]}),-1.0]])],"derivedFrom":subQ0})])]}),makeQuery(id+"F2.opRevolve","SWEPT_FACE",FACE,{"disambiguationData":[OSD([subQ0]),TDD([makeQuery(id+"F1.imprint","IMPRINT",EDGE,{"disambiguationData":[TD([[makeQuery(id+"F1.imprint","INTERSECT",VERTEX,{"derivedFrom":[subQ0,sQuery(id+"F1.wireOp",EDGE,"E22.MirrorCS")]}),1.0]])],"derivedFrom":subQ0})])]}),makeQuery(id+"F4.opExtrude","SWEPT_FACE",FACE,{"disambiguationData":[OSD([sQuery(id+"F3.wireOp",EDGE,"E34"),sQuery(id+"F3.wireOp",EDGE,"E35.MirrorCS")])]})]}),makeQuery(id+"F8.boolean.opBoolean","COPY",FACE,{"disambiguationData":[OD(1.0)],"derivedFrom":makeQuery(id+"F8.opExtrude","SWEPT_FACE",FACE,{"disambiguationData":[OSD([sQuery(id+"F7.wireOp",EDGE,"E52.MirrorCS")])]})})]});}
            var Q43;
            Q43=makeQuery(id+"F8.boolean.opBoolean","INTERSECT",EDGE,{"disambiguationData":[OD(1.0)],"derivedFrom":[makeQuery(id+"F6.opRevolve","SWEPT_FACE",FACE,{"disambiguationData":[OSD([sQuery(id+"F5.wireOp",EDGE,"E40")])]}),makeQuery(id+"F8.opExtrude","SWEPT_FACE",FACE,{"disambiguationData":[OSD([sQuery(id+"F7.wireOp",EDGE,"E52.MirrorCS")])]})]});
            var Q44;
            {var subQ0=sQuery(id+"F1.wireOp",EDGE,"E17.MirrorCS");Q44=makeQuery(id+"F9.opBoolean","INTERSECT",EDGE,{"derivedFrom":[makeQuery(id+"F4.boolean.opBoolean","MERGE",FACE,{"derivedFrom":[makeQuery(id+"F2.opRevolve","SWEPT_FACE",FACE,{"disambiguationData":[OSD([subQ0]),TDD([makeQuery(id+"F1.imprint","IMPRINT",EDGE,{"disambiguationData":[TD([[makeQuery(id+"F1.imprint","INTERSECT",VERTEX,{"derivedFrom":[sQuery(id+"F1.wireOp",EDGE,"E16.MirrorCS"),subQ0]}),-1.0]])],"derivedFrom":subQ0})])]}),makeQuery(id+"F2.opRevolve","SWEPT_FACE",FACE,{"disambiguationData":[OSD([subQ0]),TDD([makeQuery(id+"F1.imprint","IMPRINT",EDGE,{"disambiguationData":[TD([[makeQuery(id+"F1.imprint","INTERSECT",VERTEX,{"derivedFrom":[subQ0,sQuery(id+"F1.wireOp",EDGE,"E22.MirrorCS")]}),1.0]])],"derivedFrom":subQ0})])]}),makeQuery(id+"F4.opExtrude","SWEPT_FACE",FACE,{"disambiguationData":[OSD([sQuery(id+"F3.wireOp",EDGE,"E34"),sQuery(id+"F3.wireOp",EDGE,"E35.MirrorCS")])]})]}),makeQuery(id+"F8.boolean.opBoolean","COPY",FACE,{"disambiguationData":[OD(0.0)],"derivedFrom":makeQuery(id+"F8.opExtrude","SWEPT_FACE",FACE,{"disambiguationData":[OSD([sQuery(id+"F7.wireOp",EDGE,"E48")])]})})]});}
            var Q45;
            {var subQ0=sQuery(id+"F7.wireOp",EDGE,"E52.MirrorCS");Q45=makeQuery(id+"F9.opBoolean","SPLIT",EDGE,{"disambiguationData":[TD([makeQuery(id+"F6.opRevolve","SWEPT_FACE",FACE,{"disambiguationData":[OSD([sQuery(id+"F5.wireOp",EDGE,"E40")])]})])],"derivedFrom":makeQuery(id+"F8.boolean.opBoolean","COPY",EDGE,{"disambiguationData":[OD(1.0)],"derivedFrom":makeQuery(id+"F8.opExtrude","SWEPT_EDGE",EDGE,{"disambiguationData":[OSD([sQuery(id+"F7.wireOp",EDGE,"E51.MirrorCS"),subQ0])]})})});}
            var Q46;
            {var subQ0=sQuery(id+"F1.wireOp",EDGE,"E28");var subQ1=makeQuery(id+"F2.opRevolve","SWEPT_FACE",FACE,{"disambiguationData":[OSD([subQ0])]});var subQ2=sQuery(id+"F1.wireOp",EDGE,"E17.MirrorCS");var subQ3=makeQuery(id+"F4.opExtrude","SWEPT_FACE",FACE,{"disambiguationData":[OSD([sQuery(id+"F3.wireOp",EDGE,"E36.MirrorCS")])]});Q46=makeQuery(id+"F9.opBoolean","SPLIT",EDGE,{"disambiguationData":[TD([makeQuery(id+"F2.opRevolve","SWEPT_FACE",FACE,{"disambiguationData":[OSD([subQ2]),TDD([makeQuery(id+"F1.imprint","IMPRINT",EDGE,{"disambiguationData":[TD([[makeQuery(id+"F1.imprint","INTERSECT",VERTEX,{"derivedFrom":[sQuery(id+"F1.wireOp",EDGE,"E16.MirrorCS"),subQ2]}),-1.0]])],"derivedFrom":subQ2})])]}),makeQuery(id+"F2.opRevolve","SWEPT_FACE",FACE,{"disambiguationData":[OSD([subQ2]),TDD([makeQuery(id+"F1.imprint","IMPRINT",EDGE,{"disambiguationData":[TD([[makeQuery(id+"F1.imprint","INTERSECT",VERTEX,{"derivedFrom":[subQ2,sQuery(id+"F1.wireOp",EDGE,"E22.MirrorCS")]}),1.0]])],"derivedFrom":subQ2})])]}),subQ1,makeQuery(id+"F4.opExtrude","SWEPT_FACE",FACE,{"disambiguationData":[OSD([sQuery(id+"F3.wireOp",EDGE,"E34"),sQuery(id+"F3.wireOp",EDGE,"E35.MirrorCS")])]}),makeQuery(id+"F4.boolean.opBoolean","COPY",FACE,{"derivedFrom":subQ3}),makeQuery(id+"F6.opRevolve","SWEPT_FACE",FACE,{"disambiguationData":[OSD([sQuery(id+"F5.wireOp",EDGE,"E41")])]}),makeQuery(id+"F8.boolean.opBoolean","COPY",FACE,{"disambiguationData":[OD(1.0)],"derivedFrom":makeQuery(id+"F8.opExtrude","SWEPT_FACE",FACE,{"disambiguationData":[OSD([sQuery(id+"F7.wireOp",EDGE,"E52.MirrorCS")])]})})])],"derivedFrom":makeQuery(id+"F4.boolean.opBoolean","INTERSECT",EDGE,{"derivedFrom":[subQ1,subQ3]})});}
            var Q47;
            {var subQ0=sQuery(id+"F7.wireOp",EDGE,"E48");Q47=makeQuery(id+"F9.opBoolean","SPLIT",EDGE,{"disambiguationData":[TD([makeQuery(id+"F6.opRevolve","SWEPT_FACE",FACE,{"disambiguationData":[OSD([sQuery(id+"F5.wireOp",EDGE,"E40")])]})])],"derivedFrom":makeQuery(id+"F8.boolean.opBoolean","COPY",EDGE,{"disambiguationData":[OD(0.0)],"derivedFrom":makeQuery(id+"F8.opExtrude","SWEPT_EDGE",EDGE,{"disambiguationData":[OSD([subQ0,sQuery(id+"F7.wireOp",EDGE,"E50")])]})})});}
            var Q48;
            {var subQ0=sQuery(id+"F1.wireOp",EDGE,"E17.MirrorCS");Q48=makeQuery(id+"F9.opBoolean","INTERSECT",EDGE,{"derivedFrom":[makeQuery(id+"F4.boolean.opBoolean","MERGE",FACE,{"derivedFrom":[makeQuery(id+"F2.opRevolve","SWEPT_FACE",FACE,{"disambiguationData":[OSD([subQ0]),TDD([makeQuery(id+"F1.imprint","IMPRINT",EDGE,{"disambiguationData":[TD([[makeQuery(id+"F1.imprint","INTERSECT",VERTEX,{"derivedFrom":[sQuery(id+"F1.wireOp",EDGE,"E16.MirrorCS"),subQ0]}),-1.0]])],"derivedFrom":subQ0})])]}),makeQuery(id+"F2.opRevolve","SWEPT_FACE",FACE,{"disambiguationData":[OSD([subQ0]),TDD([makeQuery(id+"F1.imprint","IMPRINT",EDGE,{"disambiguationData":[TD([[makeQuery(id+"F1.imprint","INTERSECT",VERTEX,{"derivedFrom":[subQ0,sQuery(id+"F1.wireOp",EDGE,"E22.MirrorCS")]}),1.0]])],"derivedFrom":subQ0})])]}),makeQuery(id+"F4.opExtrude","SWEPT_FACE",FACE,{"disambiguationData":[OSD([sQuery(id+"F3.wireOp",EDGE,"E34"),sQuery(id+"F3.wireOp",EDGE,"E35.MirrorCS")])]})]}),makeQuery(id+"F8.boolean.opBoolean","COPY",FACE,{"disambiguationData":[OD(0.0)],"derivedFrom":makeQuery(id+"F8.opExtrude","SWEPT_FACE",FACE,{"disambiguationData":[OSD([sQuery(id+"F7.wireOp",EDGE,"E52.MirrorCS")])]})})]});}
            var Q49;
            {var subQ0=sQuery(id+"F7.wireOp",EDGE,"E52.MirrorCS");Q49=makeQuery(id+"F9.opBoolean","SPLIT",EDGE,{"disambiguationData":[TD([makeQuery(id+"F6.opRevolve","SWEPT_FACE",FACE,{"disambiguationData":[OSD([sQuery(id+"F5.wireOp",EDGE,"E40")])]})])],"derivedFrom":makeQuery(id+"F8.boolean.opBoolean","COPY",EDGE,{"disambiguationData":[OD(0.0)],"derivedFrom":makeQuery(id+"F8.opExtrude","SWEPT_EDGE",EDGE,{"disambiguationData":[OSD([sQuery(id+"F7.wireOp",EDGE,"E51.MirrorCS"),subQ0])]})})});}
            var Q50;
            {var subQ0=sQuery(id+"F7.wireOp",EDGE,"E48");Q50=makeQuery(id+"F9.opBoolean","SPLIT",EDGE,{"disambiguationData":[TD([makeQuery(id+"F6.opRevolve","SWEPT_FACE",FACE,{"disambiguationData":[OSD([sQuery(id+"F5.wireOp",EDGE,"E42")])]})])],"derivedFrom":makeQuery(id+"F8.boolean.opBoolean","COPY",EDGE,{"disambiguationData":[OD(0.0)],"derivedFrom":makeQuery(id+"F8.opExtrude","SWEPT_EDGE",EDGE,{"disambiguationData":[OSD([subQ0,sQuery(id+"F7.wireOp",EDGE,"E50")])]})})});}
            var Q51;
            Q51=makeQuery(id+"F8.boolean.opBoolean","INTERSECT",EDGE,{"disambiguationData":[OD(1.0)],"derivedFrom":[makeQuery(id+"F6.opRevolve","SWEPT_FACE",FACE,{"disambiguationData":[OSD([sQuery(id+"F5.wireOp",EDGE,"E42")])]}),makeQuery(id+"F8.opExtrude","SWEPT_FACE",FACE,{"disambiguationData":[OSD([sQuery(id+"F7.wireOp",EDGE,"E52.MirrorCS")])]})]});
            var Q52;
            {var subQ0=sQuery(id+"F7.wireOp",EDGE,"E52.MirrorCS");Q52=makeQuery(id+"F9.opBoolean","SPLIT",EDGE,{"disambiguationData":[TD([makeQuery(id+"F6.opRevolve","SWEPT_FACE",FACE,{"disambiguationData":[OSD([sQuery(id+"F5.wireOp",EDGE,"E42")])]})])],"derivedFrom":makeQuery(id+"F8.boolean.opBoolean","COPY",EDGE,{"disambiguationData":[OD(0.0)],"derivedFrom":makeQuery(id+"F8.opExtrude","SWEPT_EDGE",EDGE,{"disambiguationData":[OSD([sQuery(id+"F7.wireOp",EDGE,"E51.MirrorCS"),subQ0])]})})});}
            var Q53;
            {var subQ0=sQuery(id+"F7.wireOp",EDGE,"E52.MirrorCS");Q53=makeQuery(id+"F9.opBoolean","SPLIT",EDGE,{"disambiguationData":[TD([makeQuery(id+"F6.opRevolve","SWEPT_FACE",FACE,{"disambiguationData":[OSD([sQuery(id+"F5.wireOp",EDGE,"E42")])]})])],"derivedFrom":makeQuery(id+"F8.boolean.opBoolean","COPY",EDGE,{"disambiguationData":[OD(1.0)],"derivedFrom":makeQuery(id+"F8.opExtrude","SWEPT_EDGE",EDGE,{"disambiguationData":[OSD([sQuery(id+"F7.wireOp",EDGE,"E51.MirrorCS"),subQ0])]})})});}
            var Q54;
            {var subQ0=sQuery(id+"F1.wireOp",EDGE,"E28");var subQ1=makeQuery(id+"F2.opRevolve","SWEPT_FACE",FACE,{"disambiguationData":[OSD([subQ0])]});var subQ2=sQuery(id+"F1.wireOp",EDGE,"E17.MirrorCS");var subQ3=makeQuery(id+"F4.opExtrude","SWEPT_FACE",FACE,{"disambiguationData":[OSD([sQuery(id+"F3.wireOp",EDGE,"E31")])]});Q54=makeQuery(id+"F9.opBoolean","SPLIT",EDGE,{"disambiguationData":[TD([makeQuery(id+"F2.opRevolve","SWEPT_FACE",FACE,{"disambiguationData":[OSD([subQ2]),TDD([makeQuery(id+"F1.imprint","IMPRINT",EDGE,{"disambiguationData":[TD([[makeQuery(id+"F1.imprint","INTERSECT",VERTEX,{"derivedFrom":[sQuery(id+"F1.wireOp",EDGE,"E16.MirrorCS"),subQ2]}),-1.0]])],"derivedFrom":subQ2})])]}),makeQuery(id+"F2.opRevolve","SWEPT_FACE",FACE,{"disambiguationData":[OSD([subQ2]),TDD([makeQuery(id+"F1.imprint","IMPRINT",EDGE,{"disambiguationData":[TD([[makeQuery(id+"F1.imprint","INTERSECT",VERTEX,{"derivedFrom":[subQ2,sQuery(id+"F1.wireOp",EDGE,"E22.MirrorCS")]}),1.0]])],"derivedFrom":subQ2})])]}),subQ1,makeQuery(id+"F4.opExtrude","SWEPT_FACE",FACE,{"disambiguationData":[OSD([sQuery(id+"F3.wireOp",EDGE,"E34"),sQuery(id+"F3.wireOp",EDGE,"E35.MirrorCS")])]}),makeQuery(id+"F4.boolean.opBoolean","COPY",FACE,{"derivedFrom":subQ3}),makeQuery(id+"F6.opRevolve","SWEPT_FACE",FACE,{"disambiguationData":[OSD([sQuery(id+"F5.wireOp",EDGE,"E41")])]}),makeQuery(id+"F8.boolean.opBoolean","COPY",FACE,{"disambiguationData":[OD(0.0)],"derivedFrom":makeQuery(id+"F8.opExtrude","SWEPT_FACE",FACE,{"disambiguationData":[OSD([sQuery(id+"F7.wireOp",EDGE,"E48")])]})})])],"derivedFrom":makeQuery(id+"F4.boolean.opBoolean","INTERSECT",EDGE,{"derivedFrom":[subQ1,subQ3]})});}
            var Q55;
            {var subQ0=sQuery(id+"F1.wireOp",EDGE,"E28");var subQ1=makeQuery(id+"F2.opRevolve","SWEPT_FACE",FACE,{"disambiguationData":[OSD([subQ0])]});var subQ2=sQuery(id+"F1.wireOp",EDGE,"E17.MirrorCS");var subQ3=makeQuery(id+"F4.opExtrude","SWEPT_FACE",FACE,{"disambiguationData":[OSD([sQuery(id+"F3.wireOp",EDGE,"E36.MirrorCS")])]});Q55=makeQuery(id+"F9.opBoolean","SPLIT",EDGE,{"disambiguationData":[TD([makeQuery(id+"F2.opRevolve","SWEPT_FACE",FACE,{"disambiguationData":[OSD([subQ2]),TDD([makeQuery(id+"F1.imprint","IMPRINT",EDGE,{"disambiguationData":[TD([[makeQuery(id+"F1.imprint","INTERSECT",VERTEX,{"derivedFrom":[sQuery(id+"F1.wireOp",EDGE,"E16.MirrorCS"),subQ2]}),-1.0]])],"derivedFrom":subQ2})])]}),makeQuery(id+"F2.opRevolve","SWEPT_FACE",FACE,{"disambiguationData":[OSD([subQ2]),TDD([makeQuery(id+"F1.imprint","IMPRINT",EDGE,{"disambiguationData":[TD([[makeQuery(id+"F1.imprint","INTERSECT",VERTEX,{"derivedFrom":[subQ2,sQuery(id+"F1.wireOp",EDGE,"E22.MirrorCS")]}),1.0]])],"derivedFrom":subQ2})])]}),subQ1,makeQuery(id+"F4.opExtrude","SWEPT_FACE",FACE,{"disambiguationData":[OSD([sQuery(id+"F3.wireOp",EDGE,"E34"),sQuery(id+"F3.wireOp",EDGE,"E35.MirrorCS")])]}),makeQuery(id+"F4.boolean.opBoolean","COPY",FACE,{"derivedFrom":subQ3}),makeQuery(id+"F6.opRevolve","SWEPT_FACE",FACE,{"disambiguationData":[OSD([sQuery(id+"F5.wireOp",EDGE,"E41")])]}),makeQuery(id+"F8.boolean.opBoolean","COPY",FACE,{"disambiguationData":[OD(0.0)],"derivedFrom":makeQuery(id+"F8.opExtrude","SWEPT_FACE",FACE,{"disambiguationData":[OSD([sQuery(id+"F7.wireOp",EDGE,"E52.MirrorCS")])]})})])],"derivedFrom":makeQuery(id+"F4.boolean.opBoolean","INTERSECT",EDGE,{"derivedFrom":[subQ1,subQ3]})});}
            fillet(context, id + "F11", {"entities" : qUnion([Q0, Q1, Q2, Q3, Q4, Q5, Q6, Q7, Q8, Q9, Q10, Q11, Q12, Q13, Q14, Q15, Q16, Q17, Q18, Q19, Q20, Q21, Q22, Q23, Q24, Q25, Q26, Q27, Q28, Q29, Q30, Q31, Q32, Q33, Q34, Q35, Q36, Q37, Q38, Q39, Q40, Q41, Q42, Q43, Q44, Q45, Q46, Q47, Q48, Q49, Q50, Q51, Q52, Q53, Q54, Q55]), "radius" : 0.1 * mm, "tangentPropagation" : true, "allowEdgeOverflow" : false});
        }
    });
